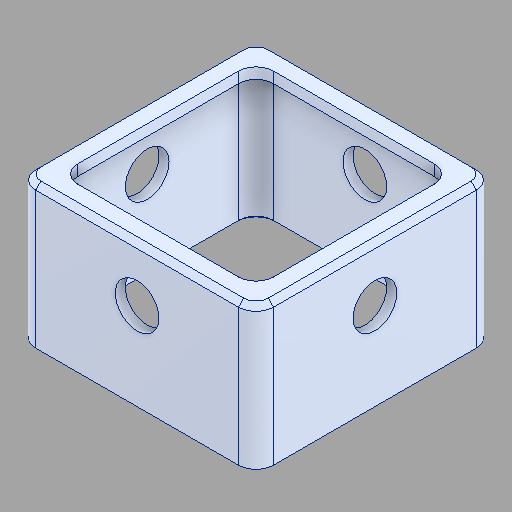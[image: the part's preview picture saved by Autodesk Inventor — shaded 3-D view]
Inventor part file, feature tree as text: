
AUTODESK INVENTOR PART (.ipt)
format: ipt  version: 2024.2 (Build 282272000, 272)  size: 151,040 bytes
history: native  units: in
note: dims shown in document units (in); Inventor stores cm internally (conversion verified against a paired STEP export)
features: chamfer x1
ambient origin geometry x8: Origin, YZ Plane, XZ Plane, XY Plane, X Axis, Y Axis, Z Axis, Center Point
bodies: Solid1 (feature_tree)
feature tree (1):
  chamfer  "Chamfer2"  [1 undecoded]
note: 1 required parameter value undecoded (feature->parameter linkage not recoverable at this tier; creation-order binding heuristic only, values carry confidence <= 0.55)
